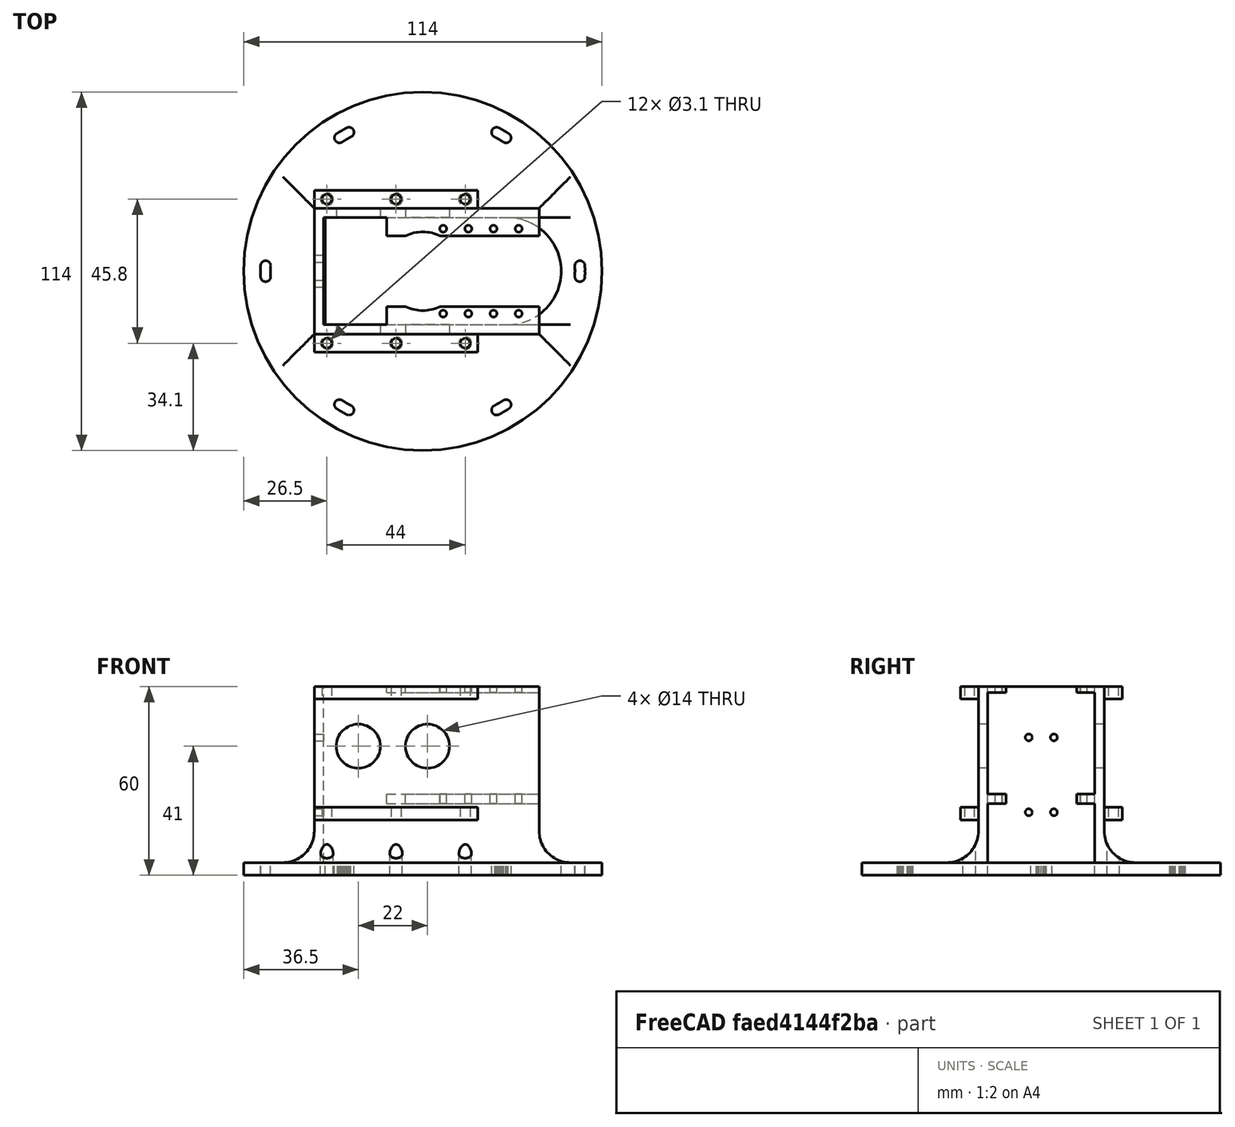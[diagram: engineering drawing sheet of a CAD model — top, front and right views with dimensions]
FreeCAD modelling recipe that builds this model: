
FCSTD DOCUMENT  (FreeCAD 0.14R2935 (Git))
Label: underside_plate
License: All rights reserved
LicenseURL: http://en.wikipedia.org/wiki/All_rights_reserved
objects: Part::Cylinder×68, Part::MultiFuse×40, Part::Box×8, Part::Cut×4, Part::Mirroring×2, Part::Fillet×1
note: 123 computed .brp shape members not serialized (recipe doc carries the construction recipe); baked Part::Feature solids carry a one-line shape summary decoded from their .brp

FEATURE [Part::Cylinder] Cylinder
  Angle = 360
  Height = 4
  Radius = 57
FEATURE [Part::Cylinder] Cylinder001
  Angle = 360
  Height = 10
  Placement = pos=(50,0,-2) rot=(0,0,1;0rad)
  Radius = 1.6
FEATURE [Part::Cylinder] Cylinder002
  Angle = 360
  Height = 10
  Placement = pos=(-50,0,-2) rot=(0,0,1;0rad)
  Radius = 1.6
FEATURE [Part::MultiFuse] Fusion
  Placement = pos=(0,0,0) rot=(0,0,1;0.017453rad)
  Shapes = -> [Cylinder001,Cylinder002]
FEATURE [Part::Cylinder] Cylinder003
  Angle = 360
  Height = 10
  Placement = pos=(50,0,-2) rot=(0,0,1;0rad)
  Radius = 1.6
FEATURE [Part::Cylinder] Cylinder004
  Angle = 360
  Height = 10
  Placement = pos=(-50,0,-2) rot=(0,0,1;0rad)
  Radius = 1.6
FEATURE [Part::MultiFuse] Fusion001
  Placement = pos=(0,0,0) rot=(0,0,1;0.034907rad)
  Shapes = -> [Cylinder003,Cylinder004]
FEATURE [Part::Cylinder] Cylinder005
  Angle = 360
  Height = 10
  Placement = pos=(50,0,-2) rot=(0,0,1;0rad)
  Radius = 1.6
FEATURE [Part::Cylinder] Cylinder006
  Angle = 360
  Height = 10
  Placement = pos=(-50,0,-2) rot=(0,0,1;0rad)
  Radius = 1.6
FEATURE [Part::MultiFuse] Fusion002
  Placement = pos=(0,0,0) rot=(0,0,-1;0.017453rad)
  Shapes = -> [Cylinder005,Cylinder006]
FEATURE [Part::Cylinder] Cylinder007
  Angle = 360
  Height = 10
  Placement = pos=(50,0,-2) rot=(0,0,1;0rad)
  Radius = 1.6
FEATURE [Part::Cylinder] Cylinder008
  Angle = 360
  Height = 10
  Placement = pos=(-50,0,-2) rot=(0,0,1;0rad)
  Radius = 1.6
FEATURE [Part::MultiFuse] Fusion003
  Placement = pos=(0,0,0) rot=(0,0,-1;0.034907rad)
  Shapes = -> [Cylinder007,Cylinder008]
FEATURE [Part::Cylinder] Cylinder009
  Angle = 360
  Height = 10
  Placement = pos=(50,0,-2) rot=(0,0,1;0rad)
  Radius = 1.6
FEATURE [Part::Cylinder] Cylinder010
  Angle = 360
  Height = 10
  Placement = pos=(-50,0,-2) rot=(0,0,1;0rad)
  Radius = 1.6
FEATURE [Part::MultiFuse] Fusion004
  Placement = pos=(0,0,0) rot=(0,0,-1;0.008727rad)
  Shapes = -> [Cylinder009,Cylinder010]
FEATURE [Part::Cylinder] Cylinder011
  Angle = 360
  Height = 10
  Placement = pos=(50,0,-2) rot=(0,0,1;0rad)
  Radius = 1.6
FEATURE [Part::Cylinder] Cylinder012
  Angle = 360
  Height = 10
  Placement = pos=(-50,0,-2) rot=(0,0,1;0rad)
  Radius = 1.6
FEATURE [Part::MultiFuse] Fusion005
  Placement = pos=(0,0,0) rot=(0,0,-1;0.02618rad)
  Shapes = -> [Cylinder011,Cylinder012]
FEATURE [Part::Cylinder] Cylinder013
  Angle = 360
  Height = 10
  Placement = pos=(50,0,-2) rot=(0,0,1;0rad)
  Radius = 1.6
FEATURE [Part::Cylinder] Cylinder014
  Angle = 360
  Height = 10
  Placement = pos=(-50,0,-2) rot=(0,0,1;0rad)
  Radius = 1.6
FEATURE [Part::MultiFuse] Fusion006
  Placement = pos=(0,0,0) rot=(0,0,1;0.02618rad)
  Shapes = -> [Cylinder013,Cylinder014]
FEATURE [Part::Cylinder] Cylinder015
  Angle = 360
  Height = 10
  Placement = pos=(50,0,-2) rot=(0,0,1;0rad)
  Radius = 1.6
FEATURE [Part::Cylinder] Cylinder016
  Angle = 360
  Height = 10
  Placement = pos=(-50,0,-2) rot=(0,0,1;0rad)
  Radius = 1.6
FEATURE [Part::MultiFuse] Fusion007
  Placement = pos=(0,0,0) rot=(0,0,1;0.008727rad)
  Shapes = -> [Cylinder015,Cylinder016]
FEATURE [Part::MultiFuse] Fusion008
  Shapes = -> [Fusion003,Fusion006,Fusion001,Fusion005,Fusion002,Fusion004,Fusion,Fusion007]
FEATURE [Part::Cylinder] Cylinder017
  Angle = 360
  Height = 10
  Placement = pos=(50,0,-2) rot=(0,0,1;0rad)
  Radius = 1.6
FEATURE [Part::Cylinder] Cylinder018
  Angle = 360
  Height = 10
  Placement = pos=(-50,0,-2) rot=(0,0,1;0rad)
  Radius = 1.6
FEATURE [Part::MultiFuse] Fusion009
  Placement = pos=(0,0,0) rot=(0,0,1;0.017453rad)
  Shapes = -> [Cylinder017,Cylinder018]
FEATURE [Part::Cylinder] Cylinder019
  Angle = 360
  Height = 10
  Placement = pos=(50,0,-2) rot=(0,0,1;0rad)
  Radius = 1.6
FEATURE [Part::Cylinder] Cylinder020
  Angle = 360
  Height = 10
  Placement = pos=(-50,0,-2) rot=(0,0,1;0rad)
  Radius = 1.6
FEATURE [Part::MultiFuse] Fusion010
  Placement = pos=(0,0,0) rot=(0,0,1;0.034907rad)
  Shapes = -> [Cylinder019,Cylinder020]
FEATURE [Part::Cylinder] Cylinder021
  Angle = 360
  Height = 10
  Placement = pos=(50,0,-2) rot=(0,0,1;0rad)
  Radius = 1.6
FEATURE [Part::Cylinder] Cylinder022
  Angle = 360
  Height = 10
  Placement = pos=(-50,0,-2) rot=(0,0,1;0rad)
  Radius = 1.6
FEATURE [Part::MultiFuse] Fusion011
  Placement = pos=(0,0,0) rot=(0,0,-1;0.017453rad)
  Shapes = -> [Cylinder021,Cylinder022]
FEATURE [Part::Cylinder] Cylinder023
  Angle = 360
  Height = 10
  Placement = pos=(50,0,-2) rot=(0,0,1;0rad)
  Radius = 1.6
FEATURE [Part::Cylinder] Cylinder024
  Angle = 360
  Height = 10
  Placement = pos=(-50,0,-2) rot=(0,0,1;0rad)
  Radius = 1.6
FEATURE [Part::MultiFuse] Fusion012
  Placement = pos=(0,0,0) rot=(0,0,-1;0.034907rad)
  Shapes = -> [Cylinder023,Cylinder024]
FEATURE [Part::Cylinder] Cylinder025
  Angle = 360
  Height = 10
  Placement = pos=(50,0,-2) rot=(0,0,1;0rad)
  Radius = 1.6
FEATURE [Part::Cylinder] Cylinder026
  Angle = 360
  Height = 10
  Placement = pos=(-50,0,-2) rot=(0,0,1;0rad)
  Radius = 1.6
FEATURE [Part::MultiFuse] Fusion013
  Placement = pos=(0,0,0) rot=(0,0,-1;0.008727rad)
  Shapes = -> [Cylinder025,Cylinder026]
FEATURE [Part::Cylinder] Cylinder027
  Angle = 360
  Height = 10
  Placement = pos=(50,0,-2) rot=(0,0,1;0rad)
  Radius = 1.6
FEATURE [Part::Cylinder] Cylinder028
  Angle = 360
  Height = 10
  Placement = pos=(-50,0,-2) rot=(0,0,1;0rad)
  Radius = 1.6
FEATURE [Part::MultiFuse] Fusion014
  Placement = pos=(0,0,0) rot=(0,0,-1;0.02618rad)
  Shapes = -> [Cylinder027,Cylinder028]
FEATURE [Part::Cylinder] Cylinder029
  Angle = 360
  Height = 10
  Placement = pos=(50,0,-2) rot=(0,0,1;0rad)
  Radius = 1.6
FEATURE [Part::Cylinder] Cylinder030
  Angle = 360
  Height = 10
  Placement = pos=(-50,0,-2) rot=(0,0,1;0rad)
  Radius = 1.6
FEATURE [Part::MultiFuse] Fusion015
  Placement = pos=(0,0,0) rot=(0,0,1;0.02618rad)
  Shapes = -> [Cylinder029,Cylinder030]
FEATURE [Part::Cylinder] Cylinder031
  Angle = 360
  Height = 10
  Placement = pos=(50,0,-2) rot=(0,0,1;0rad)
  Radius = 1.6
FEATURE [Part::Cylinder] Cylinder032
  Angle = 360
  Height = 10
  Placement = pos=(-50,0,-2) rot=(0,0,1;0rad)
  Radius = 1.6
FEATURE [Part::MultiFuse] Fusion016
  Placement = pos=(0,0,0) rot=(0,0,1;0.008727rad)
  Shapes = -> [Cylinder031,Cylinder032]
FEATURE [Part::MultiFuse] Fusion017
  Placement = pos=(0,0,0) rot=(0,0,1;1.0472rad)
  Shapes = -> [Fusion012,Fusion015,Fusion010,Fusion014,Fusion011,Fusion013,Fusion009,Fusion016]
FEATURE [Part::Cylinder] Cylinder033
  Angle = 360
  Height = 10
  Placement = pos=(50,0,-2) rot=(0,0,1;0rad)
  Radius = 1.6
FEATURE [Part::Cylinder] Cylinder034
  Angle = 360
  Height = 10
  Placement = pos=(-50,0,-2) rot=(0,0,1;0rad)
  Radius = 1.6
FEATURE [Part::MultiFuse] Fusion018
  Placement = pos=(0,0,0) rot=(0,0,1;0.017453rad)
  Shapes = -> [Cylinder033,Cylinder034]
FEATURE [Part::Cylinder] Cylinder035
  Angle = 360
  Height = 10
  Placement = pos=(50,0,-2) rot=(0,0,1;0rad)
  Radius = 1.6
FEATURE [Part::Cylinder] Cylinder036
  Angle = 360
  Height = 10
  Placement = pos=(-50,0,-2) rot=(0,0,1;0rad)
  Radius = 1.6
FEATURE [Part::MultiFuse] Fusion019
  Placement = pos=(0,0,0) rot=(0,0,1;0.034907rad)
  Shapes = -> [Cylinder035,Cylinder036]
FEATURE [Part::Cylinder] Cylinder037
  Angle = 360
  Height = 10
  Placement = pos=(50,0,-2) rot=(0,0,1;0rad)
  Radius = 1.6
FEATURE [Part::Cylinder] Cylinder038
  Angle = 360
  Height = 10
  Placement = pos=(-50,0,-2) rot=(0,0,1;0rad)
  Radius = 1.6
FEATURE [Part::MultiFuse] Fusion020
  Placement = pos=(0,0,0) rot=(0,0,-1;0.017453rad)
  Shapes = -> [Cylinder037,Cylinder038]
FEATURE [Part::Cylinder] Cylinder039
  Angle = 360
  Height = 10
  Placement = pos=(50,0,-2) rot=(0,0,1;0rad)
  Radius = 1.6
FEATURE [Part::Cylinder] Cylinder040
  Angle = 360
  Height = 10
  Placement = pos=(-50,0,-2) rot=(0,0,1;0rad)
  Radius = 1.6
FEATURE [Part::MultiFuse] Fusion021
  Placement = pos=(0,0,0) rot=(0,0,-1;0.034907rad)
  Shapes = -> [Cylinder039,Cylinder040]
FEATURE [Part::Cylinder] Cylinder041
  Angle = 360
  Height = 10
  Placement = pos=(50,0,-2) rot=(0,0,1;0rad)
  Radius = 1.6
FEATURE [Part::Cylinder] Cylinder042
  Angle = 360
  Height = 10
  Placement = pos=(-50,0,-2) rot=(0,0,1;0rad)
  Radius = 1.6
FEATURE [Part::MultiFuse] Fusion022
  Placement = pos=(0,0,0) rot=(0,0,-1;0.008727rad)
  Shapes = -> [Cylinder041,Cylinder042]
FEATURE [Part::Cylinder] Cylinder043
  Angle = 360
  Height = 10
  Placement = pos=(50,0,-2) rot=(0,0,1;0rad)
  Radius = 1.6
FEATURE [Part::Cylinder] Cylinder044
  Angle = 360
  Height = 10
  Placement = pos=(-50,0,-2) rot=(0,0,1;0rad)
  Radius = 1.6
FEATURE [Part::MultiFuse] Fusion023
  Placement = pos=(0,0,0) rot=(0,0,-1;0.02618rad)
  Shapes = -> [Cylinder043,Cylinder044]
FEATURE [Part::Cylinder] Cylinder045
  Angle = 360
  Height = 10
  Placement = pos=(50,0,-2) rot=(0,0,1;0rad)
  Radius = 1.6
FEATURE [Part::Cylinder] Cylinder046
  Angle = 360
  Height = 10
  Placement = pos=(-50,0,-2) rot=(0,0,1;0rad)
  Radius = 1.6
FEATURE [Part::MultiFuse] Fusion024
  Placement = pos=(0,0,0) rot=(0,0,1;0.02618rad)
  Shapes = -> [Cylinder045,Cylinder046]
FEATURE [Part::Cylinder] Cylinder047
  Angle = 360
  Height = 10
  Placement = pos=(50,0,-2) rot=(0,0,1;0rad)
  Radius = 1.6
FEATURE [Part::Cylinder] Cylinder048
  Angle = 360
  Height = 10
  Placement = pos=(-50,0,-2) rot=(0,0,1;0rad)
  Radius = 1.6
FEATURE [Part::MultiFuse] Fusion025
  Placement = pos=(0,0,0) rot=(0,0,1;0.008727rad)
  Shapes = -> [Cylinder047,Cylinder048]
FEATURE [Part::MultiFuse] Fusion026
  Placement = pos=(0,0,0) rot=(0,0,1;2.0944rad)
  Shapes = -> [Fusion021,Fusion024,Fusion019,Fusion023,Fusion020,Fusion022,Fusion018,Fusion025]
FEATURE [Part::MultiFuse] Fusion027
  Shapes = -> [Fusion026,Fusion017,Fusion008]
FEATURE [Part::Cylinder] Cylinder055
  Angle = 360
  Height = 10
  Placement = pos=(27,0,-2) rot=(0,0,1;0rad)
  Radius = 17
FEATURE [Part::Box] Box  label="Cube"
  Height = 3
  Length = 48.5
  Placement = pos=(-13,-20,70) rot=(0,0,1;0rad)
  Width = 3
FEATURE [Part::Box] Box001  label="Cube001"
  Height = 5.7
  Length = 52
  Placement = pos=(-30,3.6,6.1) rot=(0,0,1;0rad)
  Width = 4
FEATURE [Part::Box] Box002  label="Cube002"
  Height = 5.7
  Length = 52
  Placement = pos=(-30,42,6.1) rot=(0,0,1;0rad)
  Width = 4
FEATURE [Part::Cylinder] Cylinder056
  Angle = 360
  Height = 100
  Placement = pos=(-8,50,9) rot=(1,0,0;1.5708rad)
  Radius = 1.55
FEATURE [Part::Cylinder] Cylinder057
  Angle = 360
  Height = 100
  Placement = pos=(14,50,9) rot=(1,0,0;1.5708rad)
  Radius = 1.55
FEATURE [Part::Cylinder] Cylinder058
  Angle = 360
  Height = 100
  Placement = pos=(-30,50,9) rot=(1,0,0;1.5708rad)
  Radius = 1.55
FEATURE [Part::MultiFuse] Fusion028
  Placement = pos=(2,0,0) rot=(0,0,1;0rad)
  Shapes = -> [Cylinder058,Cylinder056,Cylinder057]
FEATURE [Part::MultiFuse] Fusion029
  Placement = pos=(-2,0,0) rot=(0,0,1;0rad)
  Shapes = -> [Box002,Box001]
FEATURE [Part::Cut] Cut
  Base = -> Fusion029
  Placement = pos=(-4,-13.9,14) rot=(1,0,0;1.5708rad)
  Tool = -> Fusion028
FEATURE [Part::Box] Box003  label="Cube003"
  Height = 56
  Length = 71.5
  Placement = pos=(-36,-20,17) rot=(0,0,1;0rad)
  Width = 3
FEATURE [Part::Box] Box004  label="Cube004"
  Height = 2
  Length = 48.5
  Placement = pos=(-13,-17,71) rot=(0,0,1;0rad)
  Width = 5.8
FEATURE [Part::Box] Box005  label="Cube005"
  Height = 3
  Length = 48.5
  Placement = pos=(-13,-17,35.8) rot=(0,0,1;0rad)
  Width = 5.8
FEATURE [Part::Cylinder] Cylinder059 .. Cylinder062  x4 (patterned run collapsed; names and placements below)
  Angle = 360
  Height = 49
  Radius = 1.1
  placements: 4 in arithmetic series — first pos=(5,-13.5,28) rot=(0,0,1;0rad), step (8,0,0), last pos=(29,-13.5,28) rot=(0,0,1;0rad)
FEATURE [Part::Cylinder] Cylinder063
  Angle = 360
  Height = 49
  Placement = pos=(-1.5,0,28) rot=(0,0,1;0rad)
  Radius = 12.5
FEATURE [Part::MultiFuse] Fusion030
  Shapes = -> [Cylinder063,Cylinder062,Cylinder061,Cylinder059,Cylinder060]
FEATURE [Part::MultiFuse] Fusion031
  Shapes = -> [Box003,Box004,Box005,Box]
FEATURE [Part::Cut] Cut001
  Base = -> Fusion031
  Placement = pos=(0,0,-13) rot=(0,0,1;0rad)
  Tool = -> Fusion030
FEATURE [Part::MultiFuse] Fusion032
  Shapes = -> [Cut001,Cut]
FEATURE [Part::Mirroring] Part__Mirroring  label="Fusion032 (Mirror #1)"
  Base = (0,0,0)
  Normal = (0,1,0)
  Source = -> Fusion032
FEATURE [Part::Box] Box006  label="Cube006"
  Height = 56
  Length = 3
  Placement = pos=(-36,-17,4) rot=(0,0,1;0rad)
  Width = 34
FEATURE [Part::Cylinder] Cylinder064
  Angle = 360
  Height = 15
  Placement = pos=(-47,-22.9,-3) rot=(0,0,1;0rad)
  Radius = 2
FEATURE [Part::Cylinder] Cylinder065
  Angle = 360
  Height = 15
  Placement = pos=(-25,-22.9,-3) rot=(0,0,1;0rad)
  Radius = 2
FEATURE [Part::Cylinder] Cylinder066
  Angle = 360
  Height = 15
  Placement = pos=(-3,-22.9,-3) rot=(0,0,1;0rad)
  Radius = 2
FEATURE [Part::MultiFuse] Fusion033
  Shapes = -> [Cylinder064,Cylinder066,Cylinder065]
FEATURE [Part::Mirroring] Part__Mirroring001  label="Fusion033 (Mirror #2)"
  Base = (0,0,0)
  Normal = (0,1,0)
  Source = -> Fusion033
FEATURE [Part::Box] Box007  label="Cube007"
  Height = 10
  Length = 58
  Placement = pos=(-31,-17,-2) rot=(0,0,1;0rad)
  Width = 34
FEATURE [Part::MultiFuse] Fusion034
  Shapes = -> [Box007,Cylinder055]
FEATURE [Part::MultiFuse] Fusion035
  Placement = pos=(16.5,0,0) rot=(0,0,1;0rad)
  Shapes = -> [Fusion033,Part__Mirroring001]
FEATURE [Part::Cylinder] Cylinder067
  Angle = 360
  Height = 100
  Placement = pos=(123.5,50,41) rot=(1,0,0;1.5708rad)
  Radius = 7
FEATURE [Part::Cylinder] Cylinder068
  Angle = 360
  Height = 100
  Placement = pos=(1.5,50,41) rot=(1,0,0;1.5708rad)
  Radius = 7
FEATURE [Part::Cylinder] Cylinder069
  Angle = 360
  Height = 100
  Placement = pos=(-20.5,50,41) rot=(1,0,0;1.5708rad)
  Radius = 7
FEATURE [Part::Cylinder] Cylinder072
  Angle = 360
  Height = 100
  Placement = pos=(0,0,0) rot=(0,1,0;1.5708rad)
  Radius = 1.1
FEATURE [Part::Cylinder] Cylinder073
  Angle = 360
  Height = 100
  Placement = pos=(0,0,8) rot=(0,1,0;1.5708rad)
  Radius = 1.1
FEATURE [Part::Cylinder] Cylinder074
  Angle = 360
  Height = 100
  Placement = pos=(0,23.8,0) rot=(0,1,0;1.5708rad)
  Radius = 1.1
FEATURE [Part::Cylinder] Cylinder075
  Angle = 360
  Height = 100
  Placement = pos=(0,23.8,8) rot=(0,1,0;1.5708rad)
  Radius = 1.1
FEATURE [Part::MultiFuse] Fusion039
  Placement = pos=(-75,4,20) rot=(1,0,0;1.5708rad)
  Shapes = -> [Cylinder075,Cylinder072,Cylinder074,Cylinder073]
FEATURE [Part::MultiFuse] Fusion041
  Placement = pos=(1.5,0,0) rot=(0,0,1;0rad)
  Shapes = -> [Part__Mirroring,Fusion032,Box006]
FEATURE [Part::Cut] Cut002
  Base = -> Cylinder
  Tool = -> Fusion027
FEATURE [Part::MultiFuse] Fusion042
  Shapes = -> [Cut002,Fusion041]
FEATURE [Part::MultiFuse] Fusion043
  Shapes = -> [Fusion035,Fusion034,Cylinder067,Cylinder068,Cylinder069,Fusion039]
FEATURE [Part::Fillet] Fillet
  Base = -> Fusion042
  Edges = 7 edges r=10: [Edge137,Edge138,Edge139,Edge140,Edge141,Edge142,Edge143]
FEATURE [Part::Cut] Cut003
  Base = -> Fillet
  Tool = -> Fusion043
